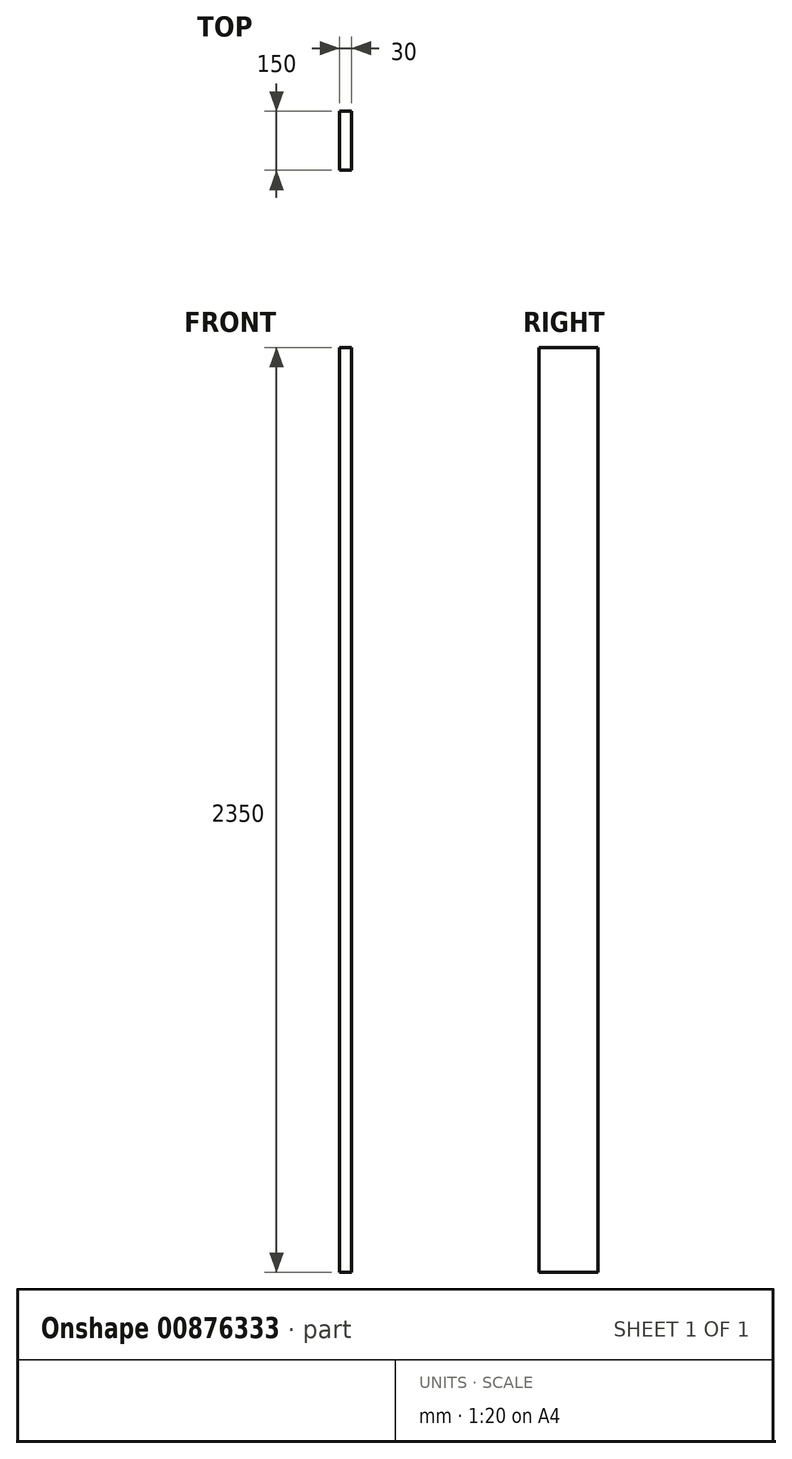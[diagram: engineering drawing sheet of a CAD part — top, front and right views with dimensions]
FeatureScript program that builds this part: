
annotation { "Feature Type Name" : "Feature", "Feature Type Description" : "" }
export const myFeature = defineFeature(function(context is Context, id is Id, definition is map)
    precondition{}
    {
        {
            var Q0;
            Q0=qCreatedBy(makeId("Top.planeOp"),FACE);
            var sketch = newSketch(context, id + "F0", { "sketchPlane" : qUnion([Q0])});
            skLineSegment(sketch, "E0", {"start": v(0, 0) * mm, "end": v(0, -150) * mm});
            skLineSegment(sketch, "E1", {"start": v(0, -150) * mm, "end": v(-30, -150) * mm});
            skLineSegment(sketch, "E2", {"start": v(-30, -150) * mm, "end": v(-30, 0) * mm});
            skLineSegment(sketch, "E3", {"start": v(-30, 0) * mm, "end": v(0, 0) * mm});
            skSolve(sketch);
        }
        {
            var Q0;
            Q0=qCreatedBy(makeId("Right.planeOp"),FACE);
            var sketch = newSketch(context, id + "F1", { "sketchPlane" : qUnion([Q0])});
            skLineSegment(sketch, "E4", {"start": v(0, 0) * mm, "end": v(0, 2350) * mm});
            skSolve(sketch);
        }
        {
            var Q0;
            Q0=makeQuery(id+"F0.imprint","IMPRINT",FACE,{"disambiguationData":[TD([[makeQuery(id+"F0.imprint","IMPRINT",EDGE,{"derivedFrom":sQuery(id+"F0.wireOp",EDGE,"E0")}),-1.0]])]});
            var Q1;
            Q1=sQuery(id+"F1.wireOp",EDGE,"E4");
            sweep(context, id + "F2", {"profiles" : qUnion([Q0]), "path" : qUnion([Q1])});
        }
    });
